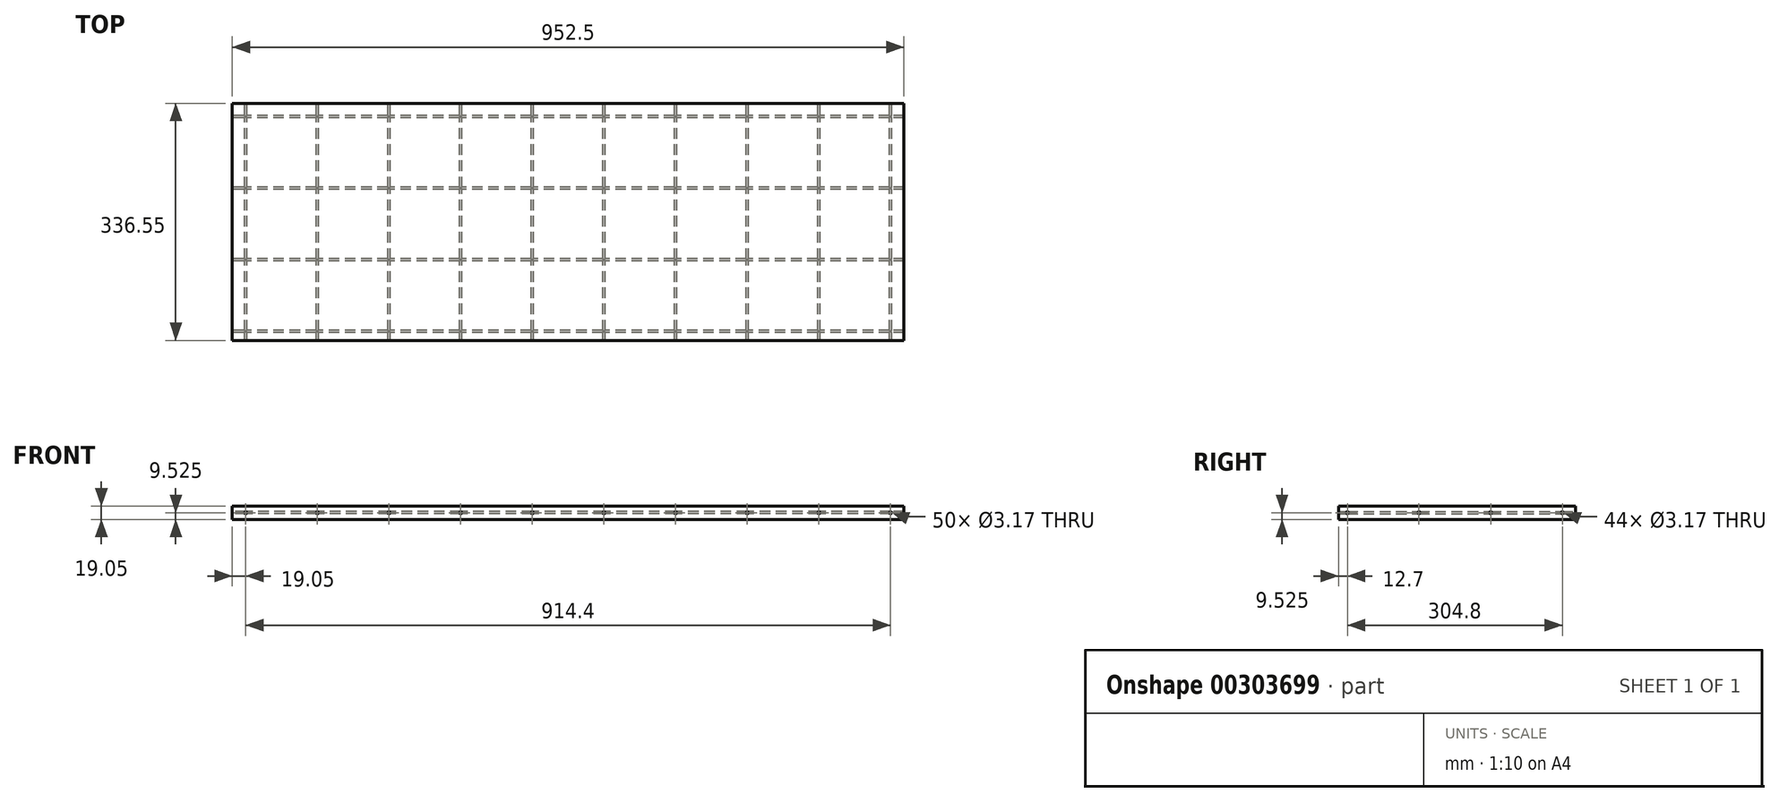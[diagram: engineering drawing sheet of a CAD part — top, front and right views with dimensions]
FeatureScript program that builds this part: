
annotation { "Feature Type Name" : "Feature", "Feature Type Description" : "" }
export const myFeature = defineFeature(function(context is Context, id is Id, definition is map)
    precondition{}
    {
        {
            var Q0;
            Q0=qCreatedBy(makeId("Top.planeOp"),FACE);
            var sketch = newSketch(context, id + "F0", { "sketchPlane" : qUnion([Q0])});
            skLineSegment(sketch, "E0.bottom", {"start": v(0, 0) * mm, "end": v(952.5, 0) * mm});
            skLineSegment(sketch, "E0.top", {"start": v(0, -336.55) * mm, "end": v(952.5, -336.55) * mm});
            skLineSegment(sketch, "E0.left", {"start": v(0, 0) * mm, "end": v(0, -336.55) * mm});
            skLineSegment(sketch, "E0.right", {"start": v(952.5, 0) * mm, "end": v(952.5, -336.55) * mm});
            skSolve(sketch);
        }
        {
            var Q0;
            Q0 = qSketchRegion(id + "F0", true);
            extrude(context, id + "F1", {"entities" : qUnion([Q0]), "oppositeDirection" : true, "depth" : 19.05 * mm});
        }
        {
            var Q0;
            Q0=qCreatedBy(makeId("Right.planeOp"),FACE);
            var sketch = newSketch(context, id + "F2", { "sketchPlane" : qUnion([Q0])});
            skCircle(sketch, "E1", {"center": v(-19.05, -9.52) * mm, "radius": 1.59 * mm});
            skCircle(sketch, "E2.1.0.0", {"center": v(-120.65, -9.52) * mm, "radius": 1.59 * mm});
            skCircle(sketch, "E2.2.0.0", {"center": v(-222.25, -9.52) * mm, "radius": 1.59 * mm});
            skCircle(sketch, "E2.3.0.0", {"center": v(-323.85, -9.52) * mm, "radius": 1.59 * mm});
            skLineSegment(sketch, "E2.direction1", {"start": v(-19.05, -9.52) * mm, "end": v(-120.65, -9.52) * mm, "construction": true});
            skSolve(sketch);
        }
        {
            var Q0;
            Q0 = qSketchRegion(id + "F2", true);
            extrude(context, id + "F3", {"entities" : qUnion([Q0]), "operationType" : NewBodyOperationType.REMOVE, "endBound" : BoundingType.THROUGH_ALL, "depth" : 25.4 * mm});
        }
        {
            var Q0;
            Q0=qCreatedBy(makeId("Front.planeOp"),FACE);
            var sketch = newSketch(context, id + "F4", { "sketchPlane" : qUnion([Q0])});
            skCircle(sketch, "E3", {"center": v(19.05, -9.53) * mm, "radius": 1.59 * mm});
            skCircle(sketch, "E4.1.0.0", {"center": v(120.65, -9.53) * mm, "radius": 1.59 * mm});
            skCircle(sketch, "E4.2.0.0", {"center": v(222.25, -9.53) * mm, "radius": 1.59 * mm});
            skCircle(sketch, "E4.3.0.0", {"center": v(323.85, -9.53) * mm, "radius": 1.59 * mm});
            skCircle(sketch, "E4.4.0.0", {"center": v(425.45, -9.53) * mm, "radius": 1.59 * mm});
            skCircle(sketch, "E4.5.0.0", {"center": v(527.05, -9.53) * mm, "radius": 1.59 * mm});
            skCircle(sketch, "E4.6.0.0", {"center": v(628.65, -9.53) * mm, "radius": 1.59 * mm});
            skCircle(sketch, "E4.7.0.0", {"center": v(730.25, -9.53) * mm, "radius": 1.59 * mm});
            skCircle(sketch, "E4.8.0.0", {"center": v(831.85, -9.53) * mm, "radius": 1.59 * mm});
            skCircle(sketch, "E4.9.0.0", {"center": v(933.45, -9.53) * mm, "radius": 1.59 * mm});
            skLineSegment(sketch, "E4.direction1", {"start": v(19.05, -9.53) * mm, "end": v(120.65, -9.53) * mm, "construction": true});
            skSolve(sketch);
        }
        {
            var Q0;
            Q0 = qSketchRegion(id + "F4", true);
            extrude(context, id + "F5", {"entities" : qUnion([Q0]), "operationType" : NewBodyOperationType.REMOVE, "endBound" : BoundingType.THROUGH_ALL, "depth" : 25.4 * mm});
        }
    });
